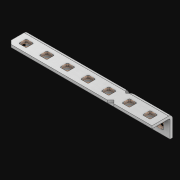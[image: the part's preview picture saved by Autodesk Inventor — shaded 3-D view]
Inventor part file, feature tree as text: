
AUTODESK INVENTOR PART (.ipt)
format: ipt  version: 2021 (Build 250183000, 183)  size: 589,312 bytes
history: native  units: in
note: dims shown in document units (in); Inventor stores cm internally (conversion verified against a paired STEP export)
features: extrude x15, other x14, sketch x3, pattern_linear x1, sheet_metal_op x1
ambient origin geometry x8: Origin, YZ Plane, XZ Plane, XY Plane, X Axis, Y Axis, Z Axis, Center Point
bodies: Solid1 (feature_tree)
feature tree (34):
  pattern_linear  "Rectangular Pattern1"  Spacing1=0.063in  [1 undecoded]
  extrude  "Extrusion1"  Depth=0.5in
  sketch  "Sketch1"  dims[d0=0.182in]
  other  "Srf1"
  sketch  "Sketch2"  dims[d1=0.063in d2=0.0in]
  other  "Srf2"
  other  "Srf3"
  other  "Srf5"
  other  "Srf7"
  other  "Srf9"
  other  "Srf11"
  other  "Srf13"
  other  "Srf4"
  other  "Srf6"
  other  "Srf8"
  other  "Srf10"
  other  "Srf12"
  other  "Srf14"
  sketch  "Sketch3"  dims[d3=0.182in d4=0.063in d5=0.0in d8=0.5in d9=14.0in d10=0.0in]
  sheet_metal_op  "Fold1"
  extrude  "ExtrusionSrf1"  Depth=0.5in TaperAngle=0.0deg
  extrude  "ExtrusionSrf2"  [1 undecoded]
  extrude  "ExtrusionSrf3"  [1 undecoded]
  extrude  "ExtrusionSrf4"  [1 undecoded]
  extrude  "ExtrusionSrf5"  [1 undecoded]
  extrude  "ExtrusionSrf6"  [1 undecoded]
  extrude  "ExtrusionSrf7"  [1 undecoded]
  extrude  "ExtrusionSrf8"  [1 undecoded]
  extrude  "ExtrusionSrf37"  [1 undecoded]
  extrude  "ExtrusionSrf38"  [1 undecoded]
  extrude  "ExtrusionSrf39"  [1 undecoded]
  extrude  "ExtrusionSrf40"  [1 undecoded]
  extrude  "ExtrusionSrf41"  [1 undecoded]
  extrude  "ExtrusionSrf42"  [1 undecoded]
note: 14 required parameter values undecoded (feature->parameter linkage not recoverable at this tier; creation-order binding heuristic only, values carry confidence <= 0.55)
